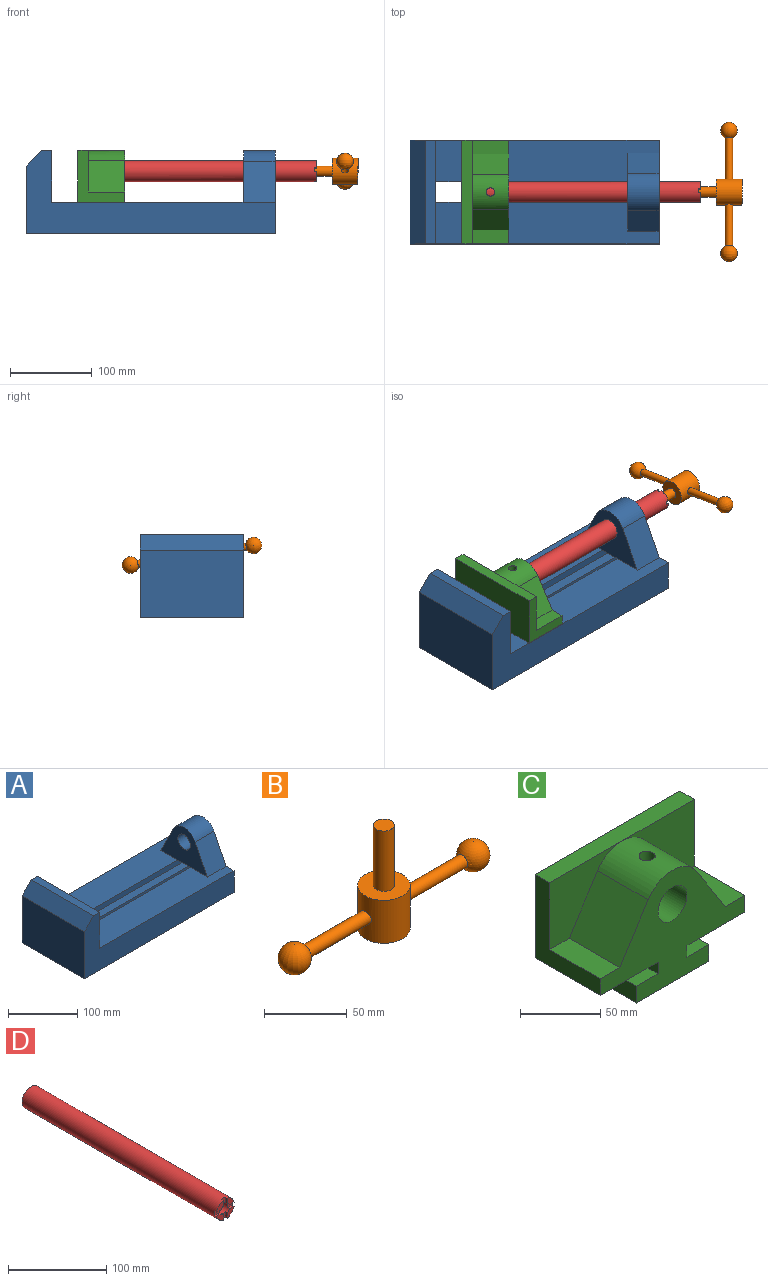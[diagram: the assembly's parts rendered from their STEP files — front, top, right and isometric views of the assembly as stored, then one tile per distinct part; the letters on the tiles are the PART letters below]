
ASSEMBLY  parts=4 mates=3
PART A: 26 faces, bbox 304.8x127x101.6 mm
  f0: plane 127x101.6mm, normal (1,0,0), area 9516.1mm2, adj f1,f2,f5,f6,f7,f8,f9,f10
  f1: plane 304.8x127mm, normal (0,0,-1), area 31774.1mm2, adj f0,f4,f5,f6,f7,f18,f24
  f2: plane 127x12.7mm, normal (0,0,1), area 1612.9mm2, adj f0,f3,f5,f6
  f3: plane 127x19.05mm, normal (-0.71,0,0.71), area 3421.5mm2, adj f2,f4,f5,f6
  f4: plane 127x82.55mm, normal (-1,0,0), area 10483.8mm2, adj f1,f3,f5,f6
  f5: plane 304.8x101.6mm, normal (0,-1,0), area 13447.6mm2, adj f0,f1,f2,f3,f4,f12,f24
  f6: plane 304.8x101.6mm, normal (0,1,0), area 13447.6mm2, adj f0,f1,f2,f3,f4,f13,f24
  f7: plane 273.05x16.51mm, normal (0,1,0), area 4508.1mm2, adj f0,f1,f8,f24
  f8: plane 273.05x19.05mm, normal (0,0,1), area 5201.6mm2, adj f0,f7,f9,f24
  f9: plane 273.05x12.7mm, normal (0,1,0), area 3467.7mm2, adj f0,f8,f10,f24
  f10: plane 273.05x19.05mm, normal (0,0,-1), area 5201.6mm2, adj f0,f9,f11,f24
  f11: plane 273.05x8.89mm, normal (0,1,0), area 2427.4mm2, adj f0,f10,f12,f22,f24
  f12: plane 273.05x50.8mm, normal (0,0,1), area 12540.3mm2, adj f0,f5,f11,f21,f24,f25
  f13: plane 273.05x50.8mm, normal (0,0,1), area 12540.3mm2, adj f0,f6,f14,f19,f24,f25
  f14: plane 273.05x8.89mm, normal (0,-1,0), area 2427.4mm2, adj f0,f13,f15,f22,f24
  f15: plane 273.05x19.05mm, normal (0,0,-1), area 5201.6mm2, adj f0,f14,f16,f24
  f16: plane 273.05x12.7mm, normal (0,-1,0), area 3467.7mm2, adj f0,f15,f17,f24
  f17: plane 273.05x19.05mm, normal (0,0,1), area 5201.6mm2, adj f0,f16,f18,f24
  f18: plane 273.05x16.51mm, normal (0,-1,0), area 4508.1mm2, adj f0,f1,f17,f24
  f19: plane 49.52x38.1mm, normal (0,0.89,0.45), area 2112.6mm2, adj f13,f20,f24,f25
  f20: cylinder r=25.4mm len=45.37mm, axis (-1,0,0), area 2137.3mm2, adj f19,f21,f24,f25
  f21: plane 49.52x38.1mm, normal (0,-0.89,0.45), area 2112.6mm2, adj f12,f20,f24,f25
  f22: plane 38.1x25.4mm, normal (0,0,-1), area 967.7mm2, adj f11,f14,f24,f25
  f23: cylinder r=12.7mm len=38.1mm, axis (-1,0,0), area 3040.2mm2, adj f24,f25
  f24: plane 127x101.6mm, normal (1,0,0), area 6815.7mm2, adj f1,f5,f6,f7,f8,f9,f10,f11
  f25: plane 95.25x63.5mm, normal (-1,0,0), area 3428.7mm2, adj f12,f13,f19,f20,f21,f22,f23
PART B: 9 faces, bbox 172.7x31.8x76.2 mm
  f0: cylinder r=4.45mm len=51.82mm, axis (-1,0,0), area 1438.5mm2, adj f2,f8
  f1: cylinder r=4.45mm len=51.88mm, axis (-1,0,0), area 1440mm2, adj f2,f7
  f2: cylinder r=15.88mm len=31.75mm, axis (0,0,1), area 3041.6mm2, adj f0,f1,f5,f6
  f3: cylinder r=6.35mm len=44.45mm, axis (0,0,-1), area 1773.5mm2, adj f4,f6
  f4: plane 12.7x12.7mm, normal (0,0,1), area 126.7mm2, adj f3
  f5: plane 31.75x31.75mm, normal (0,0,-1), area 791.7mm2, adj f2
  f6: plane 31.75x31.75mm, normal (0,0,1), area 665.1mm2, adj f2,f3
  f7: revolved ~20.32x20.21mm, area 1221.2mm2, adj f1
  f8: sphere r=10.16mm, area 1231.8mm2, adj f0
PART C: 24 faces, bbox 127x57.2x85.1 mm
  f0: plane 63.5x21.59mm, normal (0,1,0), area 1032.3mm2, adj f1,f2,f10,f11,f12,f13,f14,f16
  f1: plane 44.45x19.05mm, normal (0,0,1), area 846.8mm2, adj f0,f2,f16,f17
  f2: plane 44.45x8.89mm, normal (1,0,0), area 395.2mm2, adj f0,f1,f10,f17
  f3: plane 63.5x57.15mm, normal (1,0,0), area 1371mm2, adj f4,f10,f17,f18,f19,f20
  f4: plane 44.45x17.15mm, normal (0,0,1), area 762.1mm2, adj f3,f5,f17,f18
  f5: plane 44.45x39.07mm, normal (0.84,0,0.54), area 2060.5mm2, adj f4,f6,f17,f18
  f6: cylinder r=25.4mm len=44.45mm, axis (0,1,0), area 2182.4mm2, adj f5,f7,f17,f18,f21,f23
  f7: plane 44.45x39.07mm, normal (-0.84,0,0.54), area 2060.5mm2, adj f6,f8,f17,f21
  f8: plane 44.45x17.15mm, normal (0,0,1), area 762.1mm2, adj f7,f9,f17,f21
  f9: plane 63.5x57.15mm, normal (-1,0,0), area 1371mm2, adj f8,f10,f17,f19,f20,f21
  f10: plane 127x57.15mm, normal (0,0,-1), area 6129mm2, adj f0,f2,f3,f9,f11,f17,f19
  f11: plane 44.45x8.89mm, normal (-1,0,0), area 395.2mm2, adj f0,f10,f12,f17
  f12: plane 44.45x19.05mm, normal (0,0,1), area 846.8mm2, adj f0,f11,f13,f17
  f13: plane 44.45x12.7mm, normal (-1,0,0), area 564.5mm2, adj f0,f12,f14,f17
  f14: plane 63.5x44.45mm, normal (0,0,-1), area 2822.6mm2, adj f0,f13,f16,f17
  f15: cylinder r=12.7mm len=44.45mm, axis (0,1,0), area 3464.2mm2, adj f17,f22,f23
  f16: plane 44.45x12.7mm, normal (1,0,0), area 564.5mm2, adj f0,f1,f14,f17
  f17: plane 127x85.09mm, normal (0,-1,0), area 5140.1mm2, adj f1,f2,f3,f4,f5,f6,f7,f8
  f18: plane 63.5x50.8mm, normal (0,-1,0), area 1725mm2, adj f3,f4,f5,f6,f20
  f19: plane 127x63.5mm, normal (0,1,0), area 8064.5mm2, adj f3,f9,f10,f20
  f20: plane 127x12.7mm, normal (0,0,1), area 1612.9mm2, adj f3,f9,f18,f19,f21
  f21: plane 63.5x50.8mm, normal (0,-1,0), area 1725mm2, adj f6,f7,f8,f9,f20
  f22: plane 25.4x25.4mm, normal (0,-1,0), area 506.7mm2, adj f15
  f23: cylinder r=5.08mm len=13.76mm, axis (0,0,1), area 413.9mm2, adj f6,f15
PART D: 20 faces, bbox 25.4x279.4x25.4 mm
  f0: plane 9.9x9.9mm, normal (0,-1,0), area 62.3mm2, adj f2,f4,f12,f14
  f1: plane 9.9x9.9mm, normal (0,-1,0), area 62.3mm2, adj f2,f4,f13,f19
  f2: cylinder r=12.7mm len=279.4mm, axis (0,1,0), area 22243.2mm2, adj f0,f1,f3,f5,f6,f8,f9,f10
  f3: plane 9.9x9.9mm, normal (0,-1,0), area 62.3mm2, adj f2,f4,f9,f16
  f4: cylinder r=6.35mm len=25.4mm, axis (0,-1,0), area 960.3mm2, adj f0,f1,f3,f5,f7,f8,f9,f10
  f5: plane 9.9x9.9mm, normal (0,-1,0), area 62.3mm2, adj f2,f4,f8,f18
  f6: plane 25.4x25.4mm, normal (0,1,0), area 506.7mm2, adj f2
  f7: plane 12.7x12.7mm, normal (0,-1,0), area 126.7mm2, adj f4
  f8: plane 6.62x2.54mm, normal (-1,0,0), area 16.8mm2, adj f2,f4,f5,f10
  f9: plane 6.62x2.54mm, normal (1,0,0), area 16.8mm2, adj f2,f3,f4,f10
  f10: plane 6.88x5.08mm, normal (0,-1,0), area 32.7mm2, adj f2,f4,f8,f9
  f11: plane 6.88x5.08mm, normal (0,-1,0), area 32.7mm2, adj f2,f4,f12,f13
  f12: plane 6.62x2.54mm, normal (1,0,0), area 16.8mm2, adj f0,f2,f4,f11
  f13: plane 6.62x2.54mm, normal (-1,0,0), area 16.8mm2, adj f1,f2,f4,f11
  f14: plane 6.62x2.54mm, normal (0,0,-1), area 16.8mm2, adj f0,f2,f4,f15
  f15: plane 6.88x5.08mm, normal (0,-1,0), area 32.7mm2, adj f2,f4,f14,f16
  f16: plane 6.62x2.54mm, normal (0,0,1), area 16.8mm2, adj f2,f3,f4,f15
  f17: plane 6.88x5.08mm, normal (0,-1,0), area 32.7mm2, adj f2,f4,f18,f19
  f18: plane 6.62x2.54mm, normal (0,0,1), area 16.8mm2, adj f2,f4,f5,f17
  f19: plane 6.62x2.54mm, normal (0,0,-1), area 16.8mm2, adj f1,f2,f4,f17
PLACE A t=(-81.97,98.03,-59.99)mm fixed
PLACE B rot(axis=(-0.61,-0.52,0.61),125.4deg) t=(292.66,34.53,16.21)mm
PLACE C rot(axis=(0,0,1),90deg) t=(-5.79,34.53,-43.48)mm
PLACE D rot(axis=(-0.61,0.61,0.52),125.4deg) t=(-5.79,34.53,16.21)mm
MATE revolute D.f2 <-> C.f15  axis (-1,0,0) through (-5.79,34.53,16.21)mm
MATE fastened B.f2 <-> D.f2  axis (-1,0,0) through (248.21,34.53,16.21)mm
MATE slider C.f15 <-> A.f20  axis (1,0,0) through (-5.79,34.53,16.21)mm
